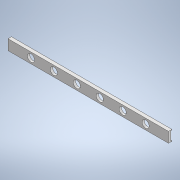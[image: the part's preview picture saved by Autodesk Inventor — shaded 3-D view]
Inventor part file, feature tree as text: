
AUTODESK INVENTOR PART (.ipt)
format: ipt  version: 2020 (Build 240168000, 168)  size: 128,512 bytes
history: native  units: mm
features: extrude x2, sketch x2
ambient origin geometry x8: Origin, YZ Plane, XZ Plane, XY Plane, X Axis, Y Axis, Z Axis, Center Point
bodies: Solide1 (feature_tree)
feature tree (4):
  extrude  "Extrusion1"  Depth=8.0mm
  extrude  "Extrusion2"  Depth=140.0mm
  sketch  "Esquisse1"
  sketch  "Esquisse2"
